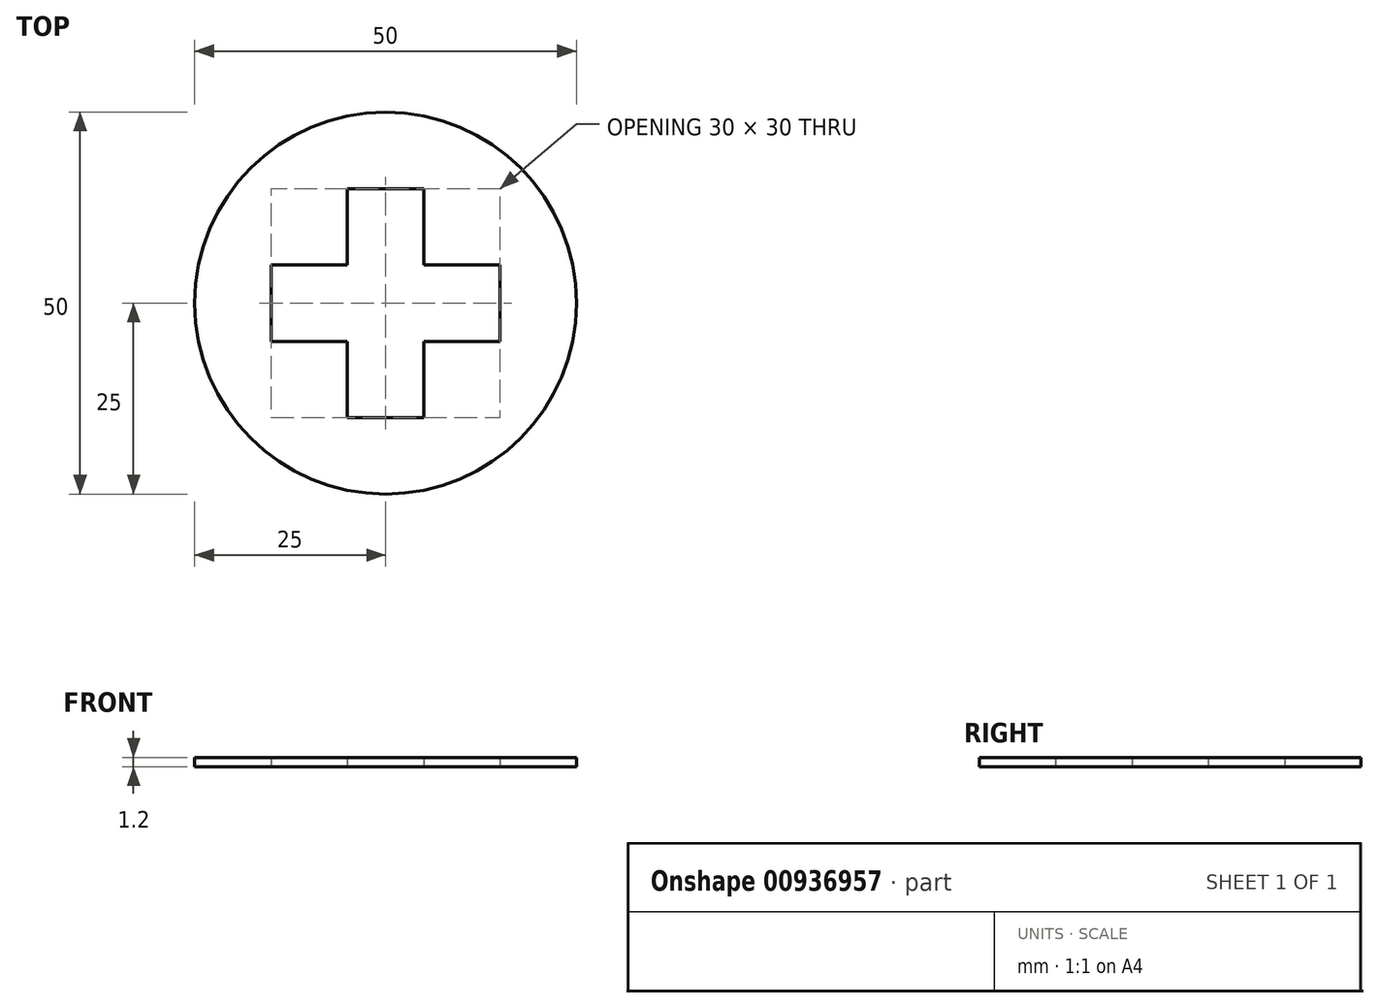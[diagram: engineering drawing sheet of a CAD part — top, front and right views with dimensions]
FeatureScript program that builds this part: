
annotation { "Feature Type Name" : "Feature", "Feature Type Description" : "" }
export const myFeature = defineFeature(function(context is Context, id is Id, definition is map)
    precondition{}
    {
        {
            var Q0;
            Q0=qCreatedBy(makeId("Top.planeOp"),FACE);
            var sketch = newSketch(context, id + "F0", { "sketchPlane" : qUnion([Q0])});
            skCircle(sketch, "E0", {"center": v(0, 0) * mm, "radius": 25 * mm});
            skLineSegment(sketch, "E1.0", {"start": v(5, 5) * mm, "end": v(5, 15) * mm});
            skLineSegment(sketch, "E2.0", {"start": v(-5, 5) * mm, "end": v(-5, 15) * mm});
            skLineSegment(sketch, "E3", {"start": v(-5, 15) * mm, "end": v(5, 15) * mm});
            skLineSegment(sketch, "E4.1.0", {"start": v(-5, -5) * mm, "end": v(-15, -5) * mm});
            skLineSegment(sketch, "E4.1.1", {"start": v(-15, -5) * mm, "end": v(-15, 5) * mm});
            skLineSegment(sketch, "E4.1.2", {"start": v(-5, 5) * mm, "end": v(-15, 5) * mm});
            skLineSegment(sketch, "E4.2.0", {"start": v(5, -5) * mm, "end": v(5, -15) * mm});
            skLineSegment(sketch, "E4.2.1", {"start": v(5, -15) * mm, "end": v(-5, -15) * mm});
            skLineSegment(sketch, "E4.2.2", {"start": v(-5, -5) * mm, "end": v(-5, -15) * mm});
            skLineSegment(sketch, "E4.3.0", {"start": v(5, 5) * mm, "end": v(15, 5) * mm});
            skLineSegment(sketch, "E4.3.1", {"start": v(15, 5) * mm, "end": v(15, -5) * mm});
            skLineSegment(sketch, "E4.3.2", {"start": v(5, -5) * mm, "end": v(15, -5) * mm});
            skSolve(sketch);
        }
        {
            var Q0;
            Q0 = qSketchRegion(id + "F0", true);
            var Q1;
            Q1=makeQuery(id+"F0.imprint","IMPRINT",FACE,{"disambiguationData":[TD([[makeQuery(id+"F0.imprint","IMPRINT",EDGE,{"derivedFrom":sQuery(id+"F0.wireOp",EDGE,"E0")}),1.0]])]});
            extrude(context, id + "F1", {"entities" : qUnion([Q0, Q1]), "depth" : 1.2 * mm, "offsetDistance" : 25 * mm});
        }
    });
